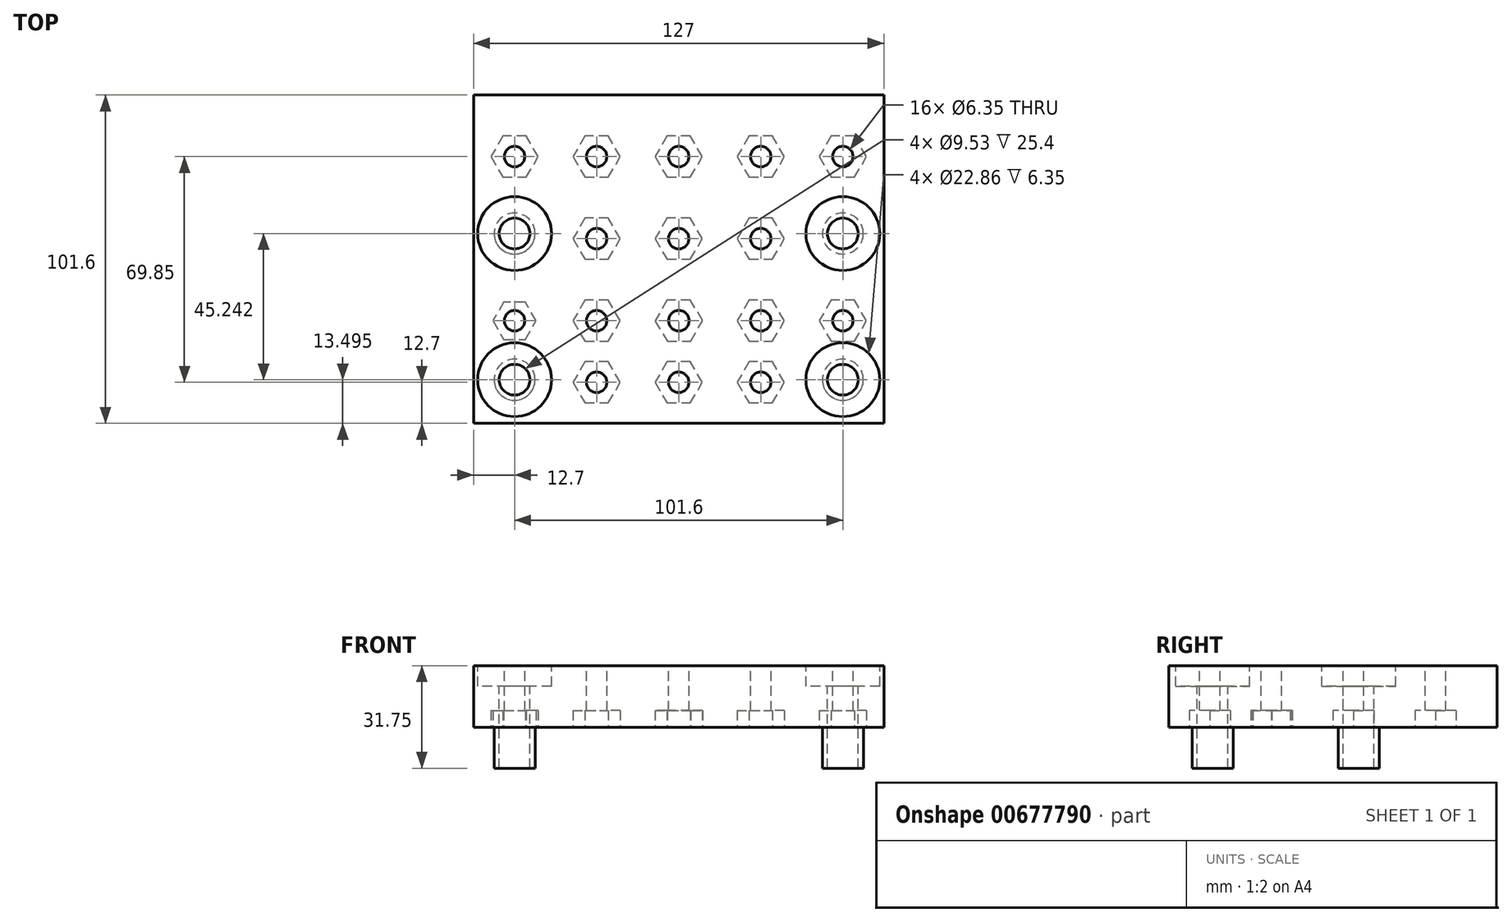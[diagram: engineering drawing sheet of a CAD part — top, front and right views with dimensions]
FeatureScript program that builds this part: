
annotation { "Feature Type Name" : "Feature", "Feature Type Description" : "" }
export const myFeature = defineFeature(function(context is Context, id is Id, definition is map)
    precondition{}
    {
        {
            var Q0;
            Q0=qCreatedBy(makeId("Top.planeOp"),FACE);
            var sketch = newSketch(context, id + "F0", { "sketchPlane" : qUnion([Q0])});
            skLineSegment(sketch, "E0.bottom", {"start": v(-63.5, 50.8) * mm, "end": v(63.5, 50.8) * mm});
            skLineSegment(sketch, "E0.top", {"start": v(-63.5, -50.8) * mm, "end": v(63.5, -50.8) * mm});
            skLineSegment(sketch, "E0.left", {"start": v(-63.5, 50.8) * mm, "end": v(-63.5, -50.8) * mm});
            skLineSegment(sketch, "E0.right", {"start": v(63.5, 50.8) * mm, "end": v(63.5, -50.8) * mm});
            skSolve(sketch);
        }
        {
            var Q0;
            Q0 = qSketchRegion(id + "F0", true);
            extrude(context, id + "F1", {"entities" : qUnion([Q0]), "oppositeDirection" : true, "depth" : 19.05 * mm, "offsetDistance" : 25.4 * mm});
        }
        {
            var Q0;
            Q0=makeQuery(id+"F1.opExtrude","CAP_FACE",FACE,{"disambiguationData":[OSD([sQuery(id+"F0.wireOp",EDGE,"E0.bottom"),sQuery(id+"F0.wireOp",EDGE,"E0.top"),sQuery(id+"F0.wireOp",EDGE,"E0.left"),sQuery(id+"F0.wireOp",EDGE,"E0.right")])],"isStart":true});
            var sketch = newSketch(context, id + "F2", { "sketchPlane" : qUnion([Q0])});
            skLineSegment(sketch, "E1.bottom", {"start": v(-50.8, 7.94) * mm, "end": v(50.8, 7.94) * mm, "construction": true});
            skLineSegment(sketch, "E1.top", {"start": v(-50.8, -37.3) * mm, "end": v(50.8, -37.3) * mm, "construction": true});
            skLineSegment(sketch, "E1.left", {"start": v(-50.8, 7.94) * mm, "end": v(-50.8, -37.3) * mm, "construction": true});
            skLineSegment(sketch, "E1.right", {"start": v(50.8, 7.94) * mm, "end": v(50.8, -37.3) * mm, "construction": true});
            skCircle(sketch, "E2", {"center": v(-50.8, 7.94) * mm, "radius": 4.76 * mm});
            skCircle(sketch, "E3", {"center": v(-50.8, -37.3) * mm, "radius": 4.76 * mm});
            skCircle(sketch, "E4", {"center": v(50.8, -37.3) * mm, "radius": 4.76 * mm});
            skCircle(sketch, "E5", {"center": v(50.8, 7.94) * mm, "radius": 4.76 * mm});
            skSolve(sketch);
        }
        {
            var Q0;
            Q0=makeQuery(id+"F2.imprint","IMPRINT",FACE,{"disambiguationData":[TD([[makeQuery(id+"F2.imprint","IMPRINT",EDGE,{"derivedFrom":sQuery(id+"F2.wireOp",EDGE,"E2")}),1.0]])]});
            var Q1;
            Q1=makeQuery(id+"F2.imprint","IMPRINT",FACE,{"disambiguationData":[TD([[makeQuery(id+"F2.imprint","IMPRINT",EDGE,{"derivedFrom":sQuery(id+"F2.wireOp",EDGE,"E5")}),1.0]])]});
            var Q2;
            Q2=makeQuery(id+"F2.imprint","IMPRINT",FACE,{"disambiguationData":[TD([[makeQuery(id+"F2.imprint","IMPRINT",EDGE,{"derivedFrom":sQuery(id+"F2.wireOp",EDGE,"E3")}),1.0]])]});
            var Q3;
            Q3=makeQuery(id+"F2.imprint","IMPRINT",FACE,{"disambiguationData":[TD([[makeQuery(id+"F2.imprint","IMPRINT",EDGE,{"derivedFrom":sQuery(id+"F2.wireOp",EDGE,"E4")}),1.0]])]});
            extrude(context, id + "F3", {"entities" : qUnion([Q0, Q1, Q2, Q3]), "operationType" : NewBodyOperationType.REMOVE, "oppositeDirection" : true, "depth" : 25.4 * mm, "offsetDistance" : 25.4 * mm});
        }
        {
            var Q0;
            Q0=makeQuery(id+"F1.opExtrude","CAP_FACE",FACE,{"disambiguationData":[OSD([sQuery(id+"F0.wireOp",EDGE,"E0.bottom"),sQuery(id+"F0.wireOp",EDGE,"E0.top"),sQuery(id+"F0.wireOp",EDGE,"E0.left"),sQuery(id+"F0.wireOp",EDGE,"E0.right")])],"isStart":true});
            var sketch = newSketch(context, id + "F4", { "sketchPlane" : qUnion([Q0])});
            skCircle(sketch, "E6", {"center": v(-50.8, 7.94) * mm, "radius": 11.43 * mm});
            skCircle(sketch, "E7", {"center": v(-50.8, -37.3) * mm, "radius": 11.43 * mm});
            skCircle(sketch, "E8", {"center": v(50.8, -37.3) * mm, "radius": 11.43 * mm});
            skCircle(sketch, "E9", {"center": v(50.8, 7.94) * mm, "radius": 11.43 * mm});
            skSolve(sketch);
        }
        {
            var Q0;
            Q0 = qSketchRegion(id + "F4", true);
            extrude(context, id + "F5", {"entities" : qUnion([Q0]), "operationType" : NewBodyOperationType.REMOVE, "oppositeDirection" : true, "depth" : 6.35 * mm, "offsetDistance" : 25.4 * mm});
        }
        {
            var Q0;
            Q0=makeQuery(id+"F1.opExtrude","CAP_FACE",FACE,{"disambiguationData":[OSD([sQuery(id+"F0.wireOp",EDGE,"E0.bottom"),sQuery(id+"F0.wireOp",EDGE,"E0.top"),sQuery(id+"F0.wireOp",EDGE,"E0.left"),sQuery(id+"F0.wireOp",EDGE,"E0.right")])],"isStart":false});
            var sketch = newSketch(context, id + "F6", { "sketchPlane" : qUnion([Q0])});
            skCircle(sketch, "E10", {"center": v(50.8, -7.94) * mm, "radius": 4.76 * mm});
            skCircle(sketch, "E11", {"center": v(50.8, 37.3) * mm, "radius": 4.76 * mm});
            skCircle(sketch, "E12", {"center": v(-50.8, 37.3) * mm, "radius": 4.76 * mm});
            skCircle(sketch, "E13", {"center": v(-50.8, -7.94) * mm, "radius": 4.76 * mm});
            skCircle(sketch, "E14", {"center": v(50.8, -7.94) * mm, "radius": 6.35 * mm});
            skCircle(sketch, "E15", {"center": v(-50.8, -7.94) * mm, "radius": 6.35 * mm});
            skCircle(sketch, "E16", {"center": v(-50.8, 37.3) * mm, "radius": 6.35 * mm});
            skCircle(sketch, "E17", {"center": v(50.8, 37.3) * mm, "radius": 6.35 * mm});
            skSolve(sketch);
        }
        {
            var Q0;
            Q0 = qSketchRegion(id + "F6", true);
            extrude(context, id + "F7", {"entities" : qUnion([Q0]), "operationType" : NewBodyOperationType.ADD, "depth" : 12.7 * mm, "offsetDistance" : 25.4 * mm});
        }
        {
            var Q0;
            Q0=makeQuery(id+"F1.opExtrude","CAP_FACE",FACE,{"disambiguationData":[OSD([sQuery(id+"F0.wireOp",EDGE,"E0.bottom"),sQuery(id+"F0.wireOp",EDGE,"E0.top"),sQuery(id+"F0.wireOp",EDGE,"E0.left"),sQuery(id+"F0.wireOp",EDGE,"E0.right")])],"isStart":true});
            var sketch = newSketch(context, id + "F8", { "sketchPlane" : qUnion([Q0])});
            skLineSegment(sketch, "E18", {"start": v(-70.31, 31.75) * mm, "end": v(73.73, 31.75) * mm, "construction": true});
            skLineSegment(sketch, "E19", {"start": v(-70.56, 6.35) * mm, "end": v(71.4, 6.35) * mm, "construction": true});
            skLineSegment(sketch, "E20", {"start": v(-69.45, -38.1) * mm, "end": v(70.17, -38.1) * mm, "construction": true});
            skLineSegment(sketch, "E21", {"start": v(-50.8, 54.6) * mm, "end": v(-50.8, -61.96) * mm, "construction": true});
            skLineSegment(sketch, "E22", {"start": v(-25.4, 55.95) * mm, "end": v(-25.4, -63.43) * mm, "construction": true});
            skLineSegment(sketch, "E23", {"start": v(25.4, 56.2) * mm, "end": v(25.4, -61.96) * mm, "construction": true});
            skLineSegment(sketch, "E24", {"start": v(50.8, 55.34) * mm, "end": v(50.8, -64.17) * mm, "construction": true});
            skLineSegment(sketch, "E25.bottom", {"start": v(-63.5, 50.8) * mm, "end": v(63.5, 50.8) * mm, "construction": true});
            skLineSegment(sketch, "E25.top", {"start": v(-63.5, -50.8) * mm, "end": v(63.5, -50.8) * mm, "construction": true});
            skLineSegment(sketch, "E25.left", {"start": v(-63.5, 50.8) * mm, "end": v(-63.5, -50.8) * mm, "construction": true});
            skLineSegment(sketch, "E25.right", {"start": v(63.5, 50.8) * mm, "end": v(63.5, -50.8) * mm, "construction": true});
            skLineSegment(sketch, "E26", {"start": v(0, 61.47) * mm, "end": v(0, -63.43) * mm, "construction": true});
            skLineSegment(sketch, "E27", {"start": v(-70.92, -19.05) * mm, "end": v(71.03, -19.05) * mm, "construction": true});
            skCircle(sketch, "E28", {"center": v(-50.8, 31.75) * mm, "radius": 3.18 * mm});
            skCircle(sketch, "E29", {"center": v(-25.4, 31.75) * mm, "radius": 3.18 * mm});
            skCircle(sketch, "E30", {"center": v(0, 31.75) * mm, "radius": 3.18 * mm});
            skCircle(sketch, "E31", {"center": v(25.4, 31.75) * mm, "radius": 3.18 * mm});
            skCircle(sketch, "E32", {"center": v(50.8, 31.75) * mm, "radius": 3.18 * mm});
            skCircle(sketch, "E33", {"center": v(-25.4, 6.35) * mm, "radius": 3.18 * mm});
            skCircle(sketch, "E34", {"center": v(0, 6.35) * mm, "radius": 3.18 * mm});
            skCircle(sketch, "E35", {"center": v(25.4, 6.35) * mm, "radius": 3.18 * mm});
            skCircle(sketch, "E36", {"center": v(-50.8, -19.05) * mm, "radius": 3.18 * mm});
            skCircle(sketch, "E37", {"center": v(-25.4, -19.05) * mm, "radius": 3.18 * mm});
            skCircle(sketch, "E38", {"center": v(0.05, -19.05) * mm, "radius": 3.18 * mm});
            skCircle(sketch, "E39", {"center": v(25.4, -19.05) * mm, "radius": 3.18 * mm});
            skCircle(sketch, "E40", {"center": v(50.8, -19.05) * mm, "radius": 3.18 * mm});
            skCircle(sketch, "E41", {"center": v(-25.4, -38.1) * mm, "radius": 3.18 * mm});
            skCircle(sketch, "E42", {"center": v(0, -38.1) * mm, "radius": 3.18 * mm});
            skCircle(sketch, "E43", {"center": v(25.4, -38.1) * mm, "radius": 3.18 * mm});
            skSolve(sketch);
        }
        {
            var Q0;
            Q0 = qSketchRegion(id + "F8", true);
            extrude(context, id + "F9", {"entities" : qUnion([Q0]), "operationType" : NewBodyOperationType.REMOVE, "oppositeDirection" : true, "depth" : 25.4 * mm, "offsetDistance" : 25.4 * mm});
        }
        {
            var Q0;
            Q0=makeQuery(id+"F1.opExtrude","CAP_FACE",FACE,{"disambiguationData":[OSD([sQuery(id+"F0.wireOp",EDGE,"E0.bottom"),sQuery(id+"F0.wireOp",EDGE,"E0.top"),sQuery(id+"F0.wireOp",EDGE,"E0.left"),sQuery(id+"F0.wireOp",EDGE,"E0.right")])],"isStart":false});
            var sketch = newSketch(context, id + "F10", { "sketchPlane" : qUnion([Q0])});
            skCircle(sketch, "E44.cCircle", {"center": v(50.8, -31.75) * mm, "radius": 6.35 * mm, "construction": true});
            skLineSegment(sketch, "E44.0", {"start": v(47.13, -25.4) * mm, "end": v(54.47, -25.4) * mm});
            skLineSegment(sketch, "E44.1", {"start": v(54.47, -25.4) * mm, "end": v(58.13, -31.75) * mm});
            skLineSegment(sketch, "E44.2", {"start": v(58.13, -31.75) * mm, "end": v(54.47, -38.1) * mm});
            skLineSegment(sketch, "E44.3", {"start": v(54.47, -38.1) * mm, "end": v(47.13, -38.1) * mm});
            skLineSegment(sketch, "E44.4", {"start": v(47.13, -38.1) * mm, "end": v(43.47, -31.75) * mm});
            skLineSegment(sketch, "E44.5", {"start": v(43.47, -31.75) * mm, "end": v(47.13, -25.4) * mm});
            skPoint(sketch, "E44.0.midPoint", {"position": v(50.8, -25.4) * mm});
            skCircle(sketch, "E45.cCircle", {"center": v(50.8, 19.05) * mm, "radius": 6.35 * mm, "construction": true});
            skLineSegment(sketch, "E45.0", {"start": v(47.13, 25.4) * mm, "end": v(54.47, 25.4) * mm});
            skLineSegment(sketch, "E45.1", {"start": v(54.47, 25.4) * mm, "end": v(58.13, 19.05) * mm});
            skLineSegment(sketch, "E45.2", {"start": v(58.13, 19.05) * mm, "end": v(54.47, 12.7) * mm});
            skLineSegment(sketch, "E45.3", {"start": v(54.47, 12.7) * mm, "end": v(47.13, 12.7) * mm});
            skLineSegment(sketch, "E45.4", {"start": v(47.13, 12.7) * mm, "end": v(43.47, 19.05) * mm});
            skLineSegment(sketch, "E45.5", {"start": v(43.47, 19.05) * mm, "end": v(47.13, 25.4) * mm});
            skPoint(sketch, "E45.0.midPoint", {"position": v(50.8, 25.4) * mm});
            skCircle(sketch, "E46.cCircle", {"center": v(25.4, -31.75) * mm, "radius": 6.35 * mm, "construction": true});
            skLineSegment(sketch, "E46.0", {"start": v(21.73, -25.4) * mm, "end": v(29.07, -25.4) * mm});
            skLineSegment(sketch, "E46.1", {"start": v(29.07, -25.4) * mm, "end": v(32.73, -31.75) * mm});
            skLineSegment(sketch, "E46.2", {"start": v(32.73, -31.75) * mm, "end": v(29.07, -38.1) * mm});
            skLineSegment(sketch, "E46.3", {"start": v(29.07, -38.1) * mm, "end": v(21.73, -38.1) * mm});
            skLineSegment(sketch, "E46.4", {"start": v(21.73, -38.1) * mm, "end": v(18.07, -31.75) * mm});
            skLineSegment(sketch, "E46.5", {"start": v(18.07, -31.75) * mm, "end": v(21.73, -25.4) * mm});
            skPoint(sketch, "E46.0.midPoint", {"position": v(25.4, -25.4) * mm});
            skCircle(sketch, "E47.cCircle", {"center": v(25.4, -6.35) * mm, "radius": 6.35 * mm, "construction": true});
            skLineSegment(sketch, "E47.0", {"start": v(21.73, 0) * mm, "end": v(29.07, 0) * mm});
            skLineSegment(sketch, "E47.1", {"start": v(29.07, 0) * mm, "end": v(32.73, -6.35) * mm});
            skLineSegment(sketch, "E47.2", {"start": v(32.73, -6.35) * mm, "end": v(29.07, -12.7) * mm});
            skLineSegment(sketch, "E47.3", {"start": v(29.07, -12.7) * mm, "end": v(21.73, -12.7) * mm});
            skLineSegment(sketch, "E47.4", {"start": v(21.73, -12.7) * mm, "end": v(18.07, -6.35) * mm});
            skLineSegment(sketch, "E47.5", {"start": v(18.07, -6.35) * mm, "end": v(21.73, 0) * mm});
            skPoint(sketch, "E47.0.midPoint", {"position": v(25.4, 0) * mm});
            skCircle(sketch, "E48.cCircle", {"center": v(25.4, 19.05) * mm, "radius": 6.35 * mm, "construction": true});
            skLineSegment(sketch, "E48.0", {"start": v(21.73, 25.4) * mm, "end": v(29.07, 25.4) * mm});
            skLineSegment(sketch, "E48.1", {"start": v(29.07, 25.4) * mm, "end": v(32.73, 19.05) * mm});
            skLineSegment(sketch, "E48.2", {"start": v(32.73, 19.05) * mm, "end": v(29.07, 12.7) * mm});
            skLineSegment(sketch, "E48.3", {"start": v(29.07, 12.7) * mm, "end": v(21.73, 12.7) * mm});
            skLineSegment(sketch, "E48.4", {"start": v(21.73, 12.7) * mm, "end": v(18.07, 19.05) * mm});
            skLineSegment(sketch, "E48.5", {"start": v(18.07, 19.05) * mm, "end": v(21.73, 25.4) * mm});
            skPoint(sketch, "E48.0.midPoint", {"position": v(25.4, 25.4) * mm});
            skCircle(sketch, "E49.cCircle", {"center": v(25.4, 38.1) * mm, "radius": 6.35 * mm, "construction": true});
            skLineSegment(sketch, "E49.0", {"start": v(21.73, 44.45) * mm, "end": v(29.07, 44.45) * mm});
            skLineSegment(sketch, "E49.1", {"start": v(29.07, 44.45) * mm, "end": v(32.73, 38.1) * mm});
            skLineSegment(sketch, "E49.2", {"start": v(32.73, 38.1) * mm, "end": v(29.07, 31.75) * mm});
            skLineSegment(sketch, "E49.3", {"start": v(29.07, 31.75) * mm, "end": v(21.73, 31.75) * mm});
            skLineSegment(sketch, "E49.4", {"start": v(21.73, 31.75) * mm, "end": v(18.07, 38.1) * mm});
            skLineSegment(sketch, "E49.5", {"start": v(18.07, 38.1) * mm, "end": v(21.73, 44.45) * mm});
            skPoint(sketch, "E49.0.midPoint", {"position": v(25.4, 44.45) * mm});
            skCircle(sketch, "E50.cCircle", {"center": v(-50.8, -31.75) * mm, "radius": 6.35 * mm, "construction": true});
            skLineSegment(sketch, "E50.0", {"start": v(-54.47, -25.4) * mm, "end": v(-47.13, -25.4) * mm});
            skLineSegment(sketch, "E50.1", {"start": v(-47.13, -25.4) * mm, "end": v(-43.47, -31.75) * mm});
            skLineSegment(sketch, "E50.2", {"start": v(-43.47, -31.75) * mm, "end": v(-47.13, -38.1) * mm});
            skLineSegment(sketch, "E50.3", {"start": v(-47.13, -38.1) * mm, "end": v(-54.47, -38.1) * mm});
            skLineSegment(sketch, "E50.4", {"start": v(-54.47, -38.1) * mm, "end": v(-58.13, -31.75) * mm});
            skLineSegment(sketch, "E50.5", {"start": v(-58.13, -31.75) * mm, "end": v(-54.47, -25.4) * mm});
            skPoint(sketch, "E50.0.midPoint", {"position": v(-50.8, -25.4) * mm});
            skCircle(sketch, "E51.cCircle", {"center": v(-50.8, 19.05) * mm, "radius": 5.76 * mm, "construction": true});
            skLineSegment(sketch, "E51.0", {"start": v(-54.13, 24.8) * mm, "end": v(-47.47, 24.8) * mm});
            skLineSegment(sketch, "E51.1", {"start": v(-47.47, 24.8) * mm, "end": v(-44.15, 19.05) * mm});
            skLineSegment(sketch, "E51.2", {"start": v(-44.15, 19.05) * mm, "end": v(-47.47, 13.3) * mm});
            skLineSegment(sketch, "E51.3", {"start": v(-47.47, 13.3) * mm, "end": v(-54.13, 13.3) * mm});
            skLineSegment(sketch, "E51.4", {"start": v(-54.13, 13.3) * mm, "end": v(-57.45, 19.05) * mm});
            skLineSegment(sketch, "E51.5", {"start": v(-57.45, 19.05) * mm, "end": v(-54.13, 24.8) * mm});
            skPoint(sketch, "E51.0.midPoint", {"position": v(-50.8, 24.8) * mm});
            skCircle(sketch, "E52.cCircle", {"center": v(-25.4, 38.1) * mm, "radius": 6.35 * mm, "construction": true});
            skLineSegment(sketch, "E52.0", {"start": v(-29.07, 44.45) * mm, "end": v(-21.73, 44.45) * mm});
            skLineSegment(sketch, "E52.1", {"start": v(-21.73, 44.45) * mm, "end": v(-18.07, 38.1) * mm});
            skLineSegment(sketch, "E52.2", {"start": v(-18.07, 38.1) * mm, "end": v(-21.73, 31.75) * mm});
            skLineSegment(sketch, "E52.3", {"start": v(-21.73, 31.75) * mm, "end": v(-29.07, 31.75) * mm});
            skLineSegment(sketch, "E52.4", {"start": v(-29.07, 31.75) * mm, "end": v(-32.73, 38.1) * mm});
            skLineSegment(sketch, "E52.5", {"start": v(-32.73, 38.1) * mm, "end": v(-29.07, 44.45) * mm});
            skPoint(sketch, "E52.0.midPoint", {"position": v(-25.4, 44.45) * mm});
            skCircle(sketch, "E53.cCircle", {"center": v(-25.4, 19.05) * mm, "radius": 6.35 * mm, "construction": true});
            skLineSegment(sketch, "E53.0", {"start": v(-29.07, 25.4) * mm, "end": v(-21.73, 25.4) * mm});
            skLineSegment(sketch, "E53.1", {"start": v(-21.73, 25.4) * mm, "end": v(-18.07, 19.05) * mm});
            skLineSegment(sketch, "E53.2", {"start": v(-18.07, 19.05) * mm, "end": v(-21.73, 12.7) * mm});
            skLineSegment(sketch, "E53.3", {"start": v(-21.73, 12.7) * mm, "end": v(-29.07, 12.7) * mm});
            skLineSegment(sketch, "E53.4", {"start": v(-29.07, 12.7) * mm, "end": v(-32.73, 19.05) * mm});
            skLineSegment(sketch, "E53.5", {"start": v(-32.73, 19.05) * mm, "end": v(-29.07, 25.4) * mm});
            skPoint(sketch, "E53.0.midPoint", {"position": v(-25.4, 25.4) * mm});
            skCircle(sketch, "E54.cCircle", {"center": v(-25.4, -6.35) * mm, "radius": 6.35 * mm, "construction": true});
            skLineSegment(sketch, "E54.0", {"start": v(-29.07, 0) * mm, "end": v(-21.73, 0) * mm});
            skLineSegment(sketch, "E54.1", {"start": v(-21.73, 0) * mm, "end": v(-18.07, -6.35) * mm});
            skLineSegment(sketch, "E54.2", {"start": v(-18.07, -6.35) * mm, "end": v(-21.73, -12.7) * mm});
            skLineSegment(sketch, "E54.3", {"start": v(-21.73, -12.7) * mm, "end": v(-29.07, -12.7) * mm});
            skLineSegment(sketch, "E54.4", {"start": v(-29.07, -12.7) * mm, "end": v(-32.73, -6.35) * mm});
            skLineSegment(sketch, "E54.5", {"start": v(-32.73, -6.35) * mm, "end": v(-29.07, 0) * mm});
            skPoint(sketch, "E54.0.midPoint", {"position": v(-25.4, 0) * mm});
            skCircle(sketch, "E55.cCircle", {"center": v(-25.4, -31.75) * mm, "radius": 6.35 * mm, "construction": true});
            skLineSegment(sketch, "E55.0", {"start": v(-29.07, -25.4) * mm, "end": v(-21.73, -25.4) * mm});
            skLineSegment(sketch, "E55.1", {"start": v(-21.73, -25.4) * mm, "end": v(-18.07, -31.75) * mm});
            skLineSegment(sketch, "E55.2", {"start": v(-18.07, -31.75) * mm, "end": v(-21.73, -38.1) * mm});
            skLineSegment(sketch, "E55.3", {"start": v(-21.73, -38.1) * mm, "end": v(-29.07, -38.1) * mm});
            skLineSegment(sketch, "E55.4", {"start": v(-29.07, -38.1) * mm, "end": v(-32.73, -31.75) * mm});
            skLineSegment(sketch, "E55.5", {"start": v(-32.73, -31.75) * mm, "end": v(-29.07, -25.4) * mm});
            skPoint(sketch, "E55.0.midPoint", {"position": v(-25.4, -25.4) * mm});
            skCircle(sketch, "E56.cCircle", {"center": v(0, -31.75) * mm, "radius": 6.35 * mm, "construction": true});
            skLineSegment(sketch, "E56.0", {"start": v(-3.67, -25.4) * mm, "end": v(3.67, -25.4) * mm});
            skLineSegment(sketch, "E56.1", {"start": v(3.67, -25.4) * mm, "end": v(7.33, -31.75) * mm});
            skLineSegment(sketch, "E56.2", {"start": v(7.33, -31.75) * mm, "end": v(3.67, -38.1) * mm});
            skLineSegment(sketch, "E56.3", {"start": v(3.67, -38.1) * mm, "end": v(-3.67, -38.1) * mm});
            skLineSegment(sketch, "E56.4", {"start": v(-3.67, -38.1) * mm, "end": v(-7.33, -31.75) * mm});
            skLineSegment(sketch, "E56.5", {"start": v(-7.33, -31.75) * mm, "end": v(-3.67, -25.4) * mm});
            skPoint(sketch, "E56.0.midPoint", {"position": v(0, -25.4) * mm});
            skCircle(sketch, "E57.cCircle", {"center": v(0, -6.35) * mm, "radius": 6.35 * mm, "construction": true});
            skLineSegment(sketch, "E57.0", {"start": v(3.67, -12.7) * mm, "end": v(-3.67, -12.7) * mm});
            skLineSegment(sketch, "E57.1", {"start": v(-3.67, -12.7) * mm, "end": v(-7.33, -6.35) * mm});
            skLineSegment(sketch, "E57.2", {"start": v(-7.33, -6.35) * mm, "end": v(-3.67, 0) * mm});
            skLineSegment(sketch, "E57.3", {"start": v(-3.67, 0) * mm, "end": v(3.67, 0) * mm});
            skLineSegment(sketch, "E57.4", {"start": v(3.67, 0) * mm, "end": v(7.33, -6.35) * mm});
            skLineSegment(sketch, "E57.5", {"start": v(7.33, -6.35) * mm, "end": v(3.67, -12.7) * mm});
            skPoint(sketch, "E57.0.midPoint", {"position": v(0, -12.7) * mm});
            skCircle(sketch, "E58.cCircle", {"center": v(0.05, 19.05) * mm, "radius": 6.35 * mm, "construction": true});
            skLineSegment(sketch, "E58.0", {"start": v(3.67, 12.67) * mm, "end": v(-3.67, 12.73) * mm});
            skLineSegment(sketch, "E58.1", {"start": v(-3.67, 12.73) * mm, "end": v(-7.28, 19.11) * mm});
            skLineSegment(sketch, "E58.2", {"start": v(-7.28, 19.11) * mm, "end": v(-3.56, 25.43) * mm});
            skLineSegment(sketch, "E58.3", {"start": v(-3.56, 25.43) * mm, "end": v(3.77, 25.37) * mm});
            skLineSegment(sketch, "E58.4", {"start": v(3.77, 25.37) * mm, "end": v(7.39, 18.99) * mm});
            skLineSegment(sketch, "E58.5", {"start": v(7.39, 18.99) * mm, "end": v(3.67, 12.67) * mm});
            skPoint(sketch, "E58.0.midPoint", {"position": v(0, 12.7) * mm});
            skCircle(sketch, "E59.cCircle", {"center": v(0, 38.1) * mm, "radius": 6.35 * mm, "construction": true});
            skLineSegment(sketch, "E59.0", {"start": v(3.67, 31.75) * mm, "end": v(-3.67, 31.75) * mm});
            skLineSegment(sketch, "E59.1", {"start": v(-3.67, 31.75) * mm, "end": v(-7.33, 38.1) * mm});
            skLineSegment(sketch, "E59.2", {"start": v(-7.33, 38.1) * mm, "end": v(-3.67, 44.45) * mm});
            skLineSegment(sketch, "E59.3", {"start": v(-3.67, 44.45) * mm, "end": v(3.67, 44.45) * mm});
            skLineSegment(sketch, "E59.4", {"start": v(3.67, 44.45) * mm, "end": v(7.33, 38.1) * mm});
            skLineSegment(sketch, "E59.5", {"start": v(7.33, 38.1) * mm, "end": v(3.67, 31.75) * mm});
            skPoint(sketch, "E59.0.midPoint", {"position": v(0, 31.75) * mm});
            skSolve(sketch);
        }
        {
            var Q0;
            Q0 = qSketchRegion(id + "F10", true);
            extrude(context, id + "F11", {"entities" : qUnion([Q0]), "operationType" : NewBodyOperationType.REMOVE, "oppositeDirection" : true, "depth" : 5.16 * mm, "offsetDistance" : 25.4 * mm});
        }
    });
